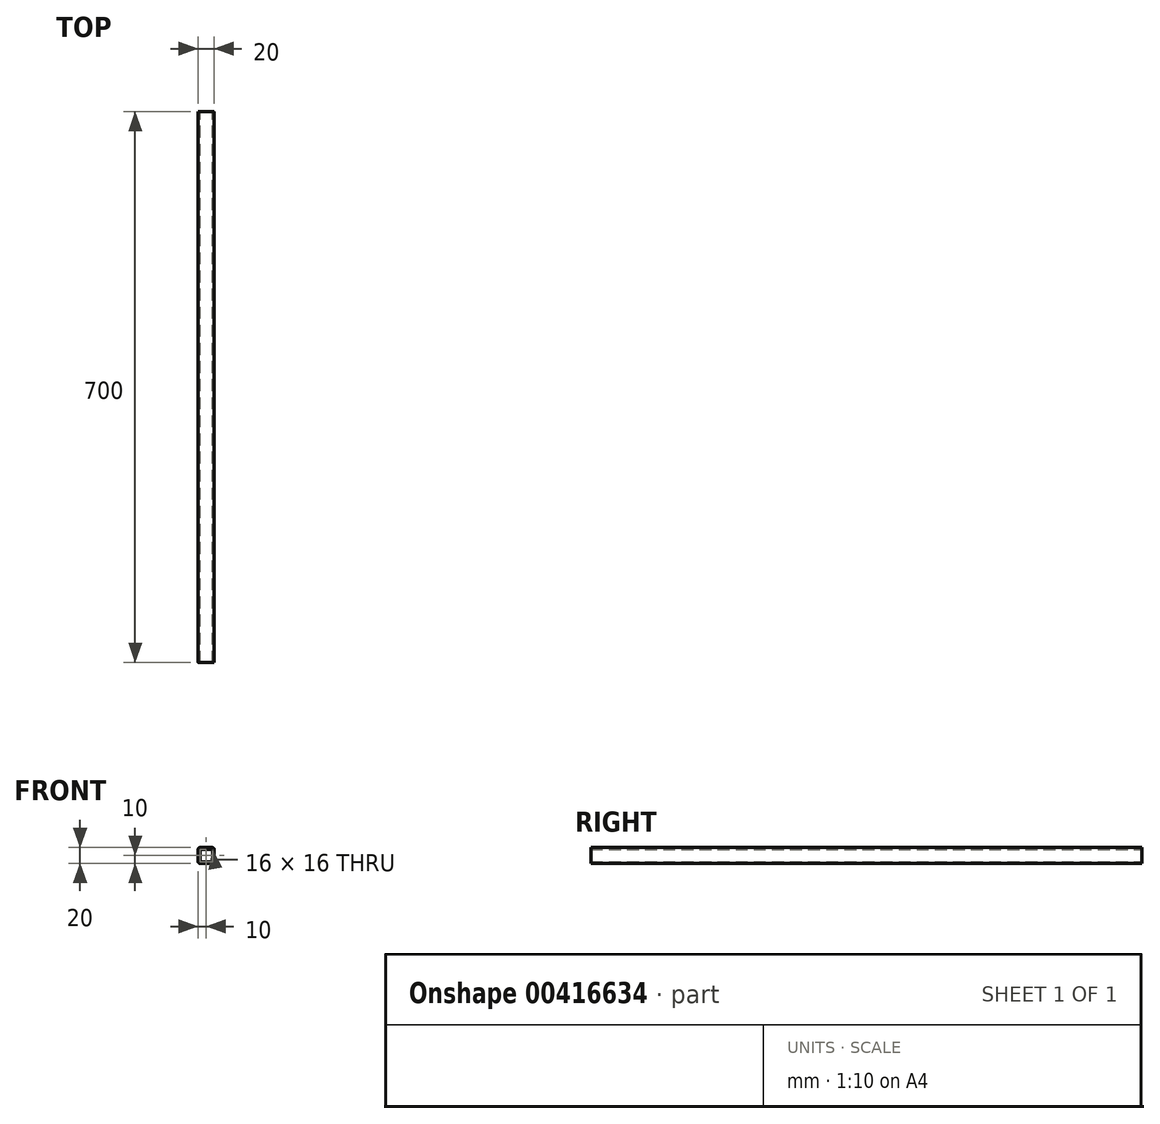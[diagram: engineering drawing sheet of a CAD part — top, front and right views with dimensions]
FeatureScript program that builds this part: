
annotation { "Feature Type Name" : "Feature", "Feature Type Description" : "" }
export const myFeature = defineFeature(function(context is Context, id is Id, definition is map)
    precondition{}
    {
        {
            var Q0;
            Q0=qCreatedBy(makeId("Front.planeOp"),FACE);
            var sketch = newSketch(context, id + "F0", { "sketchPlane" : qUnion([Q0])});
            skLineSegment(sketch, "E0.bottom", {"start": v(0, 0) * mm, "end": v(20, 0) * mm});
            skLineSegment(sketch, "E0.top", {"start": v(0, -20) * mm, "end": v(20, -20) * mm});
            skLineSegment(sketch, "E0.left", {"start": v(0, 0) * mm, "end": v(0, -20) * mm});
            skLineSegment(sketch, "E0.right", {"start": v(20, 0) * mm, "end": v(20, -20) * mm});
            skLineSegment(sketch, "E1", {"start": v(20, 0) * mm, "end": v(0, -20) * mm, "construction": true});
            skLineSegment(sketch, "E2.bottom", {"start": v(2, -2) * mm, "end": v(18, -2) * mm});
            skLineSegment(sketch, "E2.top", {"start": v(2, -18) * mm, "end": v(18, -18) * mm});
            skLineSegment(sketch, "E2.left", {"start": v(2, -2) * mm, "end": v(2, -18) * mm});
            skLineSegment(sketch, "E2.right", {"start": v(18, -2) * mm, "end": v(18, -18) * mm});
            skSolve(sketch);
        }
        {
            var Q0;
            Q0 = qSketchRegion(id + "F0", true);
            extrude(context, id + "F1", {"entities" : qUnion([Q0]), "depth" : 700 * mm});
        }
        {
            var Q0;
            Q0=makeQuery(id+"F1.opExtrude","SWEPT_EDGE",EDGE,{"disambiguationData":[OSD([sQuery(id+"F0.wireOp",EDGE,"E0.bottom"),sQuery(id+"F0.wireOp",EDGE,"E0.right")])]});
            var Q1;
            Q1=makeQuery(id+"F1.opExtrude","SWEPT_EDGE",EDGE,{"disambiguationData":[OSD([sQuery(id+"F0.wireOp",EDGE,"E0.bottom"),sQuery(id+"F0.wireOp",EDGE,"E0.left")])]});
            var Q2;
            Q2=makeQuery(id+"F1.opExtrude","SWEPT_EDGE",EDGE,{"disambiguationData":[OSD([sQuery(id+"F0.wireOp",EDGE,"E0.top"),sQuery(id+"F0.wireOp",EDGE,"E0.left")])]});
            var Q3;
            Q3=makeQuery(id+"F1.opExtrude","SWEPT_EDGE",EDGE,{"disambiguationData":[OSD([sQuery(id+"F0.wireOp",EDGE,"E0.top"),sQuery(id+"F0.wireOp",EDGE,"E0.right")])]});
            fillet(context, id + "F2", {"entities" : qUnion([Q0, Q1, Q2, Q3]), "radius" : 2 * mm, "tangentPropagation" : true, "allowEdgeOverflow" : false});
        }
    });
